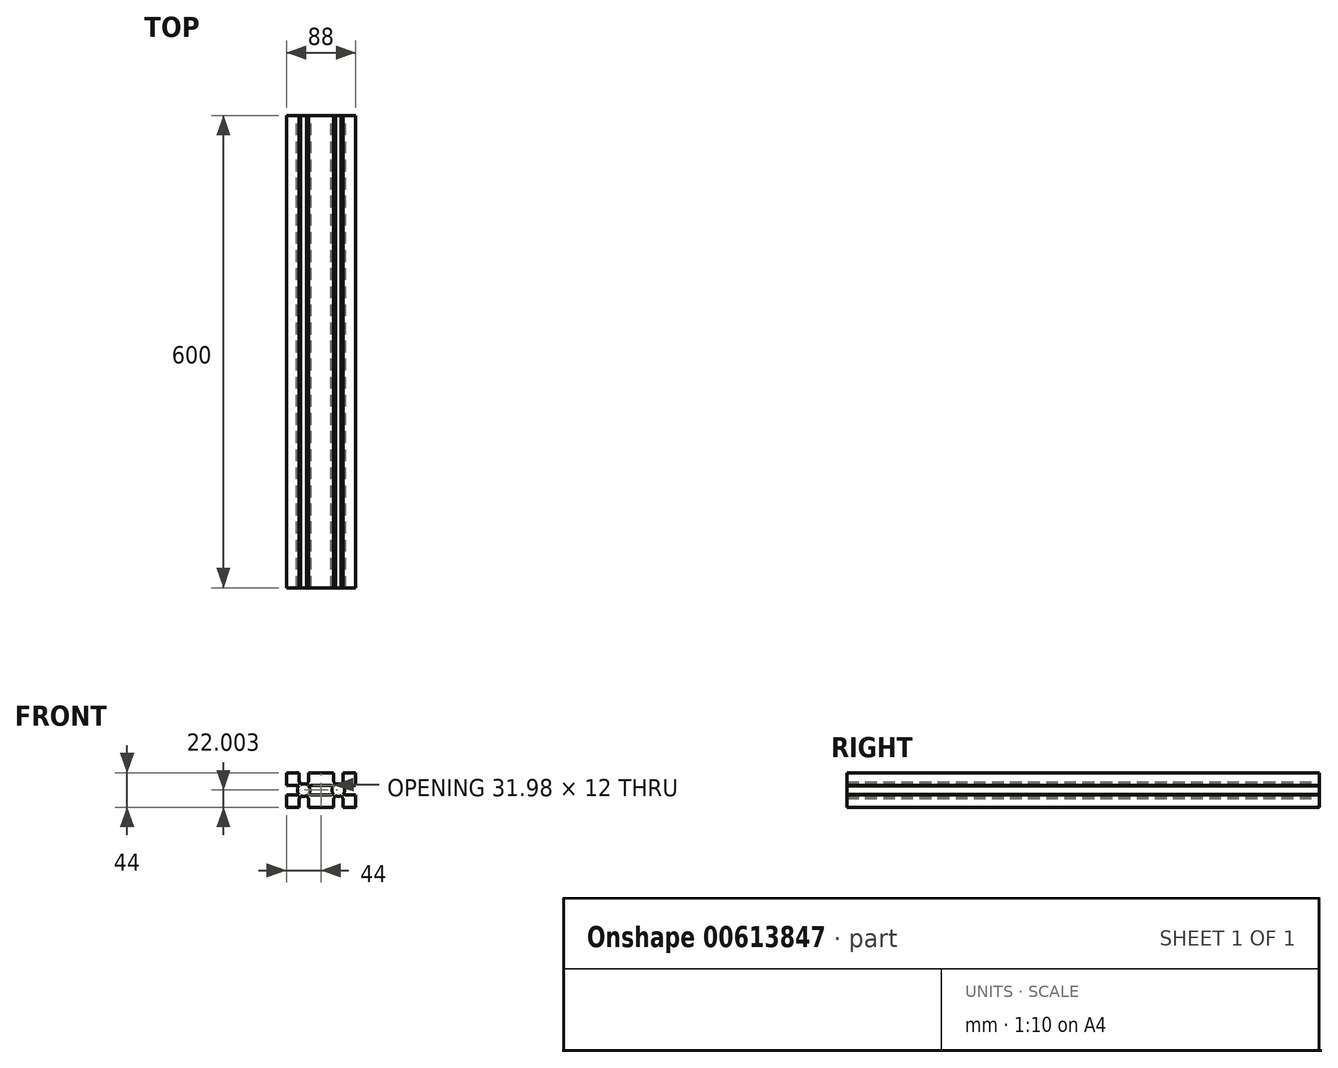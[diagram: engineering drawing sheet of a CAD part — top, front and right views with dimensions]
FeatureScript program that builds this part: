
annotation { "Feature Type Name" : "Feature", "Feature Type Description" : "" }
export const myFeature = defineFeature(function(context is Context, id is Id, definition is map)
    precondition{}
    {
        {
            var Q0;
            Q0=qCreatedBy(makeId("Front.planeOp"),FACE);
            var sketch = newSketch(context, id + "F0", { "sketchPlane" : qUnion([Q0])});
            skPoint(sketch, "E0.middle", {"position": v(19.95, 29.02) * mm});
            skLineSegment(sketch, "E1.bottom", {"start": v(41.95, 7.02) * mm, "end": v(25.95, 7.02) * mm});
            skLineSegment(sketch, "E1.left", {"start": v(41.95, 7.02) * mm, "end": v(41.95, 23.02) * mm});
            skCircle(sketch, "E2", {"center": v(19.95, 29.02) * mm, "radius": 8 * mm});
            skPoint(sketch, "E3", {"position": v(41.95, 29.02) * mm});
            skPoint(sketch, "E3.positionSnap0", {"position": v(41.95, 15.02) * mm});
            skPoint(sketch, "E4", {"position": v(19.95, 7.02) * mm});
            skLineSegment(sketch, "E5", {"start": v(25.95, 7.02) * mm, "end": v(25.95, 18.6) * mm});
            skLineSegment(sketch, "E6", {"start": v(25.95, 18.6) * mm, "end": v(23.61, 21.9) * mm});
            skLineSegment(sketch, "E7", {"start": v(41.95, 23.02) * mm, "end": v(29.08, 23.02) * mm});
            skLineSegment(sketch, "E8", {"start": v(29.08, 23.02) * mm, "end": v(25.96, 23.75) * mm});
            skLineSegment(sketch, "E9.MirrorCS", {"start": v(13.95, 7.02) * mm, "end": v(13.95, 18.6) * mm});
            skLineSegment(sketch, "E10.MirrorCS", {"start": v(-2.05, 7.02) * mm, "end": v(13.95, 7.02) * mm});
            skLineSegment(sketch, "E11.MirrorCS", {"start": v(-2.05, 7.02) * mm, "end": v(-2.05, 23.02) * mm});
            skLineSegment(sketch, "E12.MirrorCS", {"start": v(-2.05, 23.02) * mm, "end": v(10.82, 23.02) * mm});
            skLineSegment(sketch, "E13.MirrorCS", {"start": v(13.95, 18.6) * mm, "end": v(16.29, 21.9) * mm});
            skLineSegment(sketch, "E14.MirrorCS", {"start": v(10.82, 23.02) * mm, "end": v(13.94, 23.75) * mm});
            skLineSegment(sketch, "E15.MirrorCS", {"start": v(41.95, 51.02) * mm, "end": v(41.95, 35.02) * mm});
            skLineSegment(sketch, "E16.MirrorCS", {"start": v(41.95, 35.02) * mm, "end": v(29.08, 35.02) * mm});
            skLineSegment(sketch, "E17.MirrorCS", {"start": v(41.95, 51.02) * mm, "end": v(25.95, 51.02) * mm});
            skLineSegment(sketch, "E18.MirrorCS", {"start": v(25.95, 51.02) * mm, "end": v(25.95, 39.45) * mm});
            skLineSegment(sketch, "E19.MirrorCS", {"start": v(25.95, 39.45) * mm, "end": v(23.61, 36.14) * mm});
            skLineSegment(sketch, "E20.MirrorCS", {"start": v(29.08, 35.02) * mm, "end": v(25.96, 34.3) * mm});
            skLineSegment(sketch, "E21.MirrorCS", {"start": v(13.95, 39.45) * mm, "end": v(16.29, 36.14) * mm});
            skLineSegment(sketch, "E22.MirrorCS", {"start": v(10.82, 35.02) * mm, "end": v(13.94, 34.3) * mm});
            skLineSegment(sketch, "E23.MirrorCS", {"start": v(13.95, 51.02) * mm, "end": v(13.95, 39.45) * mm});
            skLineSegment(sketch, "E24.MirrorCS", {"start": v(-2.05, 51.02) * mm, "end": v(13.95, 51.02) * mm});
            skLineSegment(sketch, "E25.MirrorCS", {"start": v(-2.05, 51.02) * mm, "end": v(-2.05, 35.02) * mm});
            skLineSegment(sketch, "E26.MirrorCS", {"start": v(-2.05, 35.02) * mm, "end": v(10.82, 35.02) * mm});
            skPoint(sketch, "E27.MirrorP", {"position": v(-24.05, 29.02) * mm});
            skLineSegment(sketch, "E28.MirrorCS", {"start": v(-2.05, 51.02) * mm, "end": v(-18.05, 51.02) * mm});
            skLineSegment(sketch, "E29.MirrorCS", {"start": v(-2.05, 35.02) * mm, "end": v(-14.92, 35.02) * mm});
            skLineSegment(sketch, "E30.MirrorCS", {"start": v(-18.05, 51.02) * mm, "end": v(-18.05, 39.45) * mm});
            skLineSegment(sketch, "E31.MirrorCS", {"start": v(-18.05, 39.45) * mm, "end": v(-20.39, 36.14) * mm});
            skLineSegment(sketch, "E32.MirrorCS", {"start": v(-14.92, 35.02) * mm, "end": v(-18.04, 34.3) * mm});
            skCircle(sketch, "E33.MirrorC", {"center": v(-24.05, 29.02) * mm, "radius": 8 * mm});
            skLineSegment(sketch, "E34.MirrorCS", {"start": v(-30.05, 39.45) * mm, "end": v(-27.71, 36.14) * mm});
            skLineSegment(sketch, "E35.MirrorCS", {"start": v(-33.18, 35.02) * mm, "end": v(-30.06, 34.3) * mm});
            skLineSegment(sketch, "E36.MirrorCS", {"start": v(-30.05, 51.02) * mm, "end": v(-30.05, 39.45) * mm});
            skLineSegment(sketch, "E37.MirrorCS", {"start": v(-46.05, 51.02) * mm, "end": v(-30.05, 51.02) * mm});
            skLineSegment(sketch, "E38.MirrorCS", {"start": v(-46.05, 51.02) * mm, "end": v(-46.05, 35.02) * mm});
            skLineSegment(sketch, "E39.MirrorCS", {"start": v(-46.05, 35.02) * mm, "end": v(-33.18, 35.02) * mm});
            skLineSegment(sketch, "E40.MirrorCS", {"start": v(-2.05, 23.02) * mm, "end": v(-14.92, 23.02) * mm});
            skLineSegment(sketch, "E41.MirrorCS", {"start": v(-14.92, 23.02) * mm, "end": v(-18.04, 23.75) * mm});
            skLineSegment(sketch, "E42.MirrorCS", {"start": v(-18.05, 18.6) * mm, "end": v(-20.39, 21.9) * mm});
            skLineSegment(sketch, "E43.MirrorCS", {"start": v(-18.05, 7.02) * mm, "end": v(-18.05, 18.6) * mm});
            skLineSegment(sketch, "E44.MirrorCS", {"start": v(-2.05, 7.02) * mm, "end": v(-18.05, 7.02) * mm});
            skLineSegment(sketch, "E45.MirrorCS", {"start": v(-46.05, 23.02) * mm, "end": v(-33.18, 23.02) * mm});
            skLineSegment(sketch, "E46.MirrorCS", {"start": v(-33.18, 23.02) * mm, "end": v(-30.06, 23.75) * mm});
            skLineSegment(sketch, "E47.MirrorCS", {"start": v(-30.05, 18.6) * mm, "end": v(-27.71, 21.9) * mm});
            skLineSegment(sketch, "E48.MirrorCS", {"start": v(-30.05, 7.02) * mm, "end": v(-30.05, 18.6) * mm});
            skLineSegment(sketch, "E49.MirrorCS", {"start": v(-46.05, 7.02) * mm, "end": v(-30.05, 7.02) * mm});
            skLineSegment(sketch, "E50.MirrorCS", {"start": v(-46.05, 7.02) * mm, "end": v(-46.05, 23.02) * mm});
            skSolve(sketch);
        }
        {
            var Q0;
            Q0 = qSketchRegion(id + "F0", true);
            extrude(context, id + "F1", {"entities" : qUnion([Q0]), "depth" : 600 * mm, "offsetDistance" : 25 * mm});
        }
    });
